# Revit family: PRD_FrankeWS_SpprtRls_AngleGrabRail_CNTX20WL_CNTX20WR
name_source: partatom
category: Specialty Equipment
revit_build: Autodesk Revit 2018 (Build: 20190510_1515(x64)
units: mm (PartAtom-declared; Revit-internal decimal feet)

## family parameters
Cut with Voids When Loaded = No
Host = Face
OmniClass Number = 23.40.20.21
OmniClass Title = Toilet and Bath Specialties
Part Type = Normal
Room Calculation Point = No
Round Connector Dimension = Use Diameter
Shared = No

## types (2) — shared parameters
AssetType = Fixed
BendingAngle = 90.00 degree
Category = Pr_40_20_76_84, Support rails
Color = no color
Default Elevation = 750 mm  [stored 2.46063 ft]
Description = 90° angle grab rail for wall mounting, stainless steel, surface satin finished, rough polishing for better surface feel, 32 mm pipe diameter, material thickness 1.2 mm, wall distance 82 mm, with three stainless steel covers for hidden mounting, includes stainless steel screws and dowels.
DurationUnit = year
Features = stainless steel, surface satin finished
Finish = satin finished
GrabRailMaterial = PRD_AR_StainlessSteel_SatinFinished
GrossWeight = 2.25 kg
HiddenFixing = Yes
Hinged = No
IfcExportAs = IfcFurnitureType
IfcExportType = USERDEFINED
IntegralAccessories = incl. stainless steel screws and dowels
IsBuiltIn = TRUE
MainColor = stainless steel
Manufacturer = KWC Group AG
ManufacturerName = KWC Group AG
ManufacturerURL = www.kwc.com
Material = stainless steel
MaterialCode = 1.4301
MaterialThickness = 1.20 mm
NBSDescription = Support rails
NBSReference = 45-35-72/360
NetWeight = 2.18 kg
NominalDepth = 82 mm  [stored 0.269029 ft]
NominalHeight = 1328 mm  [stored 4.35696 ft]
NominalWidth = 678 mm  [stored 2.22441 ft]
PipeDiameter = 32  [stored 0.104987 ft]
ProductInformation = https://pim.kwc.com
Size = 678 x 1328 x 82 mm
TypeOfFixing = Screw
TypeOfGrabRail = Angle bar
TypeOfMounting = Wall mounting
URL = www.kwc.com
Uniclass2015Code = Pr_40_20_76_84
Uniclass2015Title = Support rails
Uniclass2015Version = Products v1.10
Version = 1
WarrantyDurationUnit = year

## per-type parameters (varying)
| type | BIMObjectName | CNTX20WL | CNTX20WR | Direction | ModelNumber | Name |
| CNTX20WL | PRD_AR_SupportRails_AngleGrabRail_CNTX20WL | Yes | No | Left | 2030038220 | Angle Grab Rail CNTX20WL |
| CNTX20WR | PRD_AR_SupportRails_AngleGrabRail_CNTX20WR | No | Yes | Right | 2030038221 | Angle Grab Rail CNTX20WR |

note: column(s) folded — value = type name in every type: Model, ModelReference

note: [stored X ft] marks values corroborated as IEEE doubles in the binary element streams (Revit-internal decimal feet)

## geometry (parser evidence)
native form markers: Sweep x6
no freeform markers — native parametric forms only
